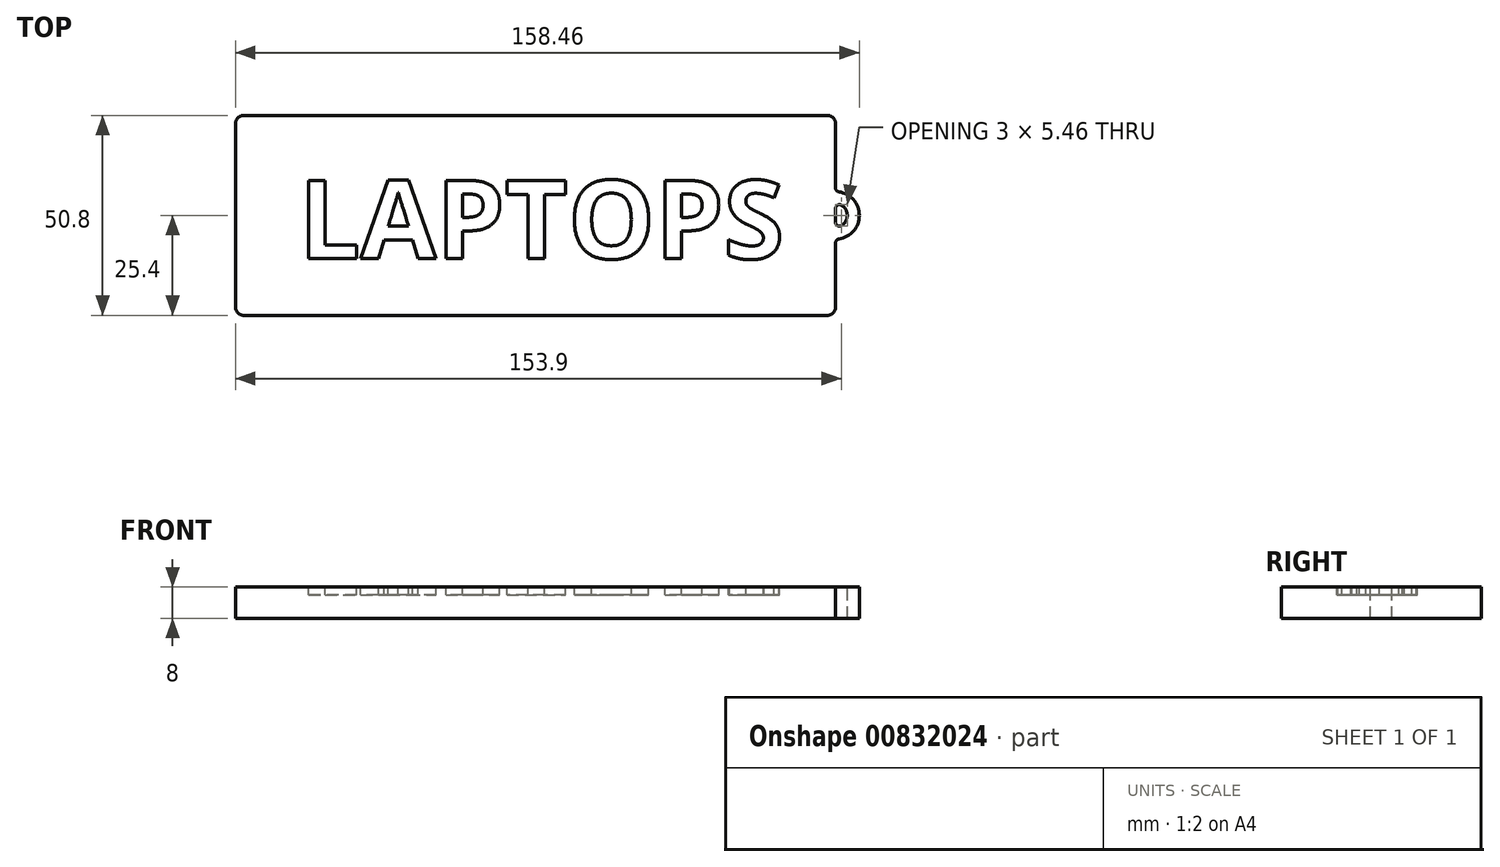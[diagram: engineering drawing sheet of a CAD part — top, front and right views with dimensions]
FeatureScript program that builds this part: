
annotation { "Feature Type Name" : "Feature", "Feature Type Description" : "" }
export const myFeature = defineFeature(function(context is Context, id is Id, definition is map)
    precondition{}
    {
        {
            var Q0;
            Q0=qCreatedBy(makeId("Top.planeOp"),FACE);
            var sketch = newSketch(context, id + "F0", { "sketchPlane" : qUnion([Q0])});
            skLineSegment(sketch, "E0.bottom", {"start": v(-2, 0) * mm, "end": v(-150.4, 0) * mm});
            skLineSegment(sketch, "E0.top", {"start": v(-2, 50.8) * mm, "end": v(-150.4, 50.8) * mm});
            skLineSegment(sketch, "E0.left", {"start": v(0, 0) * mm, "end": v(0, 19.34) * mm});
            skLineSegment(sketch, "E0.right", {"start": v(-152.4, 2) * mm, "end": v(-152.4, 48.8) * mm});
            skLineSegment(sketch, "E1", {"start": v(0, 2) * mm, "end": v(0, 18.42) * mm});
            skArc(sketch, "E2", {"start": v(1.5, 22.8) * mm, "mid": v(3, 25.4) * mm, "end": v(1.5, 28) * mm});
            skArc(sketch, "E3", {"start": v(0.86, 19.4) * mm, "mid": v(6.06, 25.4) * mm, "end": v(0.86, 31.4) * mm});
            skPoint(sketch, "E4.end.orphan", {"position": v(3, 25.4) * mm});
            skLineSegment(sketch, "E5.trimOffspring", {"start": v(0, 32.38) * mm, "end": v(0, 48.8) * mm});
            skPoint(sketch, "E6.visualSharp", {"position": v(-152.4, 50.8) * mm});
            skArc(sketch, "E6.filletArc", {"start": v(-150.4, 50.8) * mm, "mid": v(-151.81, 50.21) * mm, "end": v(-152.4, 48.8) * mm});
            skPoint(sketch, "E7.visualSharp", {"position": v(-152.4, 0) * mm});
            skArc(sketch, "E7.filletArc", {"start": v(-152.4, 2) * mm, "mid": v(-151.81, 0.59) * mm, "end": v(-150.4, 0) * mm});
            skPoint(sketch, "E8.visualSharp", {"position": v(0, 0) * mm});
            skArc(sketch, "E8.filletArc", {"start": v(-2, 0) * mm, "mid": v(-0.59, 0.59) * mm, "end": v(0, 2) * mm});
            skPoint(sketch, "E9.visualSharp", {"position": v(0, 50.8) * mm});
            skArc(sketch, "E9.filletArc", {"start": v(0, 48.8) * mm, "mid": v(-0.59, 50.21) * mm, "end": v(-2, 50.8) * mm});
            skPoint(sketch, "E10.visualSharp", {"position": v(0, 31.46) * mm});
            skArc(sketch, "E10.filletArc", {"start": v(0, 32.38) * mm, "mid": v(0.24, 31.73) * mm, "end": v(0.86, 31.4) * mm});
            skPoint(sketch, "E11.visualSharp", {"position": v(0, 19.34) * mm});
            skArc(sketch, "E11.filletArc", {"start": v(0.86, 19.4) * mm, "mid": v(0.24, 19.07) * mm, "end": v(0, 18.42) * mm});
            skLineSegment(sketch, "E12", {"start": v(0, 25.4) * mm, "end": v(0, 27.13) * mm});
            skPoint(sketch, "E13.visualSharp", {"position": v(0, 28.4) * mm});
            skArc(sketch, "E13.filletArc", {"start": v(1.5, 28) * mm, "mid": v(0.5, 28) * mm, "end": v(0, 27.13) * mm});
            skLineSegment(sketch, "E14", {"start": v(0, 25.4) * mm, "end": v(0, 23.67) * mm});
            skPoint(sketch, "E15.visualSharp", {"position": v(0, 22.4) * mm});
            skArc(sketch, "E15.filletArc", {"start": v(0, 23.67) * mm, "mid": v(0.5, 22.8) * mm, "end": v(1.5, 22.8) * mm});
            skSolve(sketch);
        }
        {
            var Q0;
            Q0=makeQuery(id+"F0.imprint","IMPRINT",FACE,{"disambiguationData":[TD([[makeQuery(id+"F0.imprint","IMPRINT",EDGE,{"derivedFrom":sQuery(id+"F0.wireOp",EDGE,"E0.bottom")}),-1.0]])]});
            extrude(context, id + "F1", {"entities" : qUnion([Q0]), "oppositeDirection" : true, "depth" : 8 * mm, "offsetDistance" : 25 * mm});
        }
        {
            var Q0;
            Q0=makeQuery(id+"F1.opExtrude","CAP_FACE",FACE,{"disambiguationData":[OSD([sQuery(id+"F0.wireOp",EDGE,"E0.bottom"),sQuery(id+"F0.wireOp",EDGE,"E0.top"),sQuery(id+"F0.wireOp",EDGE,"E0.right"),sQuery(id+"F0.wireOp",EDGE,"E1"),sQuery(id+"F0.wireOp",EDGE,"E2"),sQuery(id+"F0.wireOp",EDGE,"E3"),sQuery(id+"F0.wireOp",EDGE,"E5.trimOffspring"),sQuery(id+"F0.wireOp",EDGE,"E6.filletArc"),sQuery(id+"F0.wireOp",EDGE,"E7.filletArc"),sQuery(id+"F0.wireOp",EDGE,"E8.filletArc"),sQuery(id+"F0.wireOp",EDGE,"E9.filletArc"),sQuery(id+"F0.wireOp",EDGE,"E10.filletArc"),sQuery(id+"F0.wireOp",EDGE,"E11.filletArc"),sQuery(id+"F0.wireOp",EDGE,"E12"),sQuery(id+"F0.wireOp",EDGE,"E13.filletArc"),sQuery(id+"F0.wireOp",EDGE,"E14"),sQuery(id+"F0.wireOp",EDGE,"E15.filletArc")])],"isStart":true});
            var sketch = newSketch(context, id + "F2", { "sketchPlane" : qUnion([Q0])});
            skText(sketch, "E16", { "text": "LAPTOPS", "fontName": "OpenSans-Bold.ttf"});
            const initialGuessF2  = {"E16": [-0.13635, 0.01442, 1, 0, 0.02]};
            skSetInitialGuess(sketch, initialGuessF2);
            skSolve(sketch);
        }
        {
            var Q0;
            Q0 = qSketchRegion(id + "F2", true);
            extrude(context, id + "F3", {"entities" : qUnion([Q0]), "operationType" : NewBodyOperationType.REMOVE, "oppositeDirection" : true, "depth" : 2 * mm, "offsetDistance" : 25 * mm});
        }
    });
